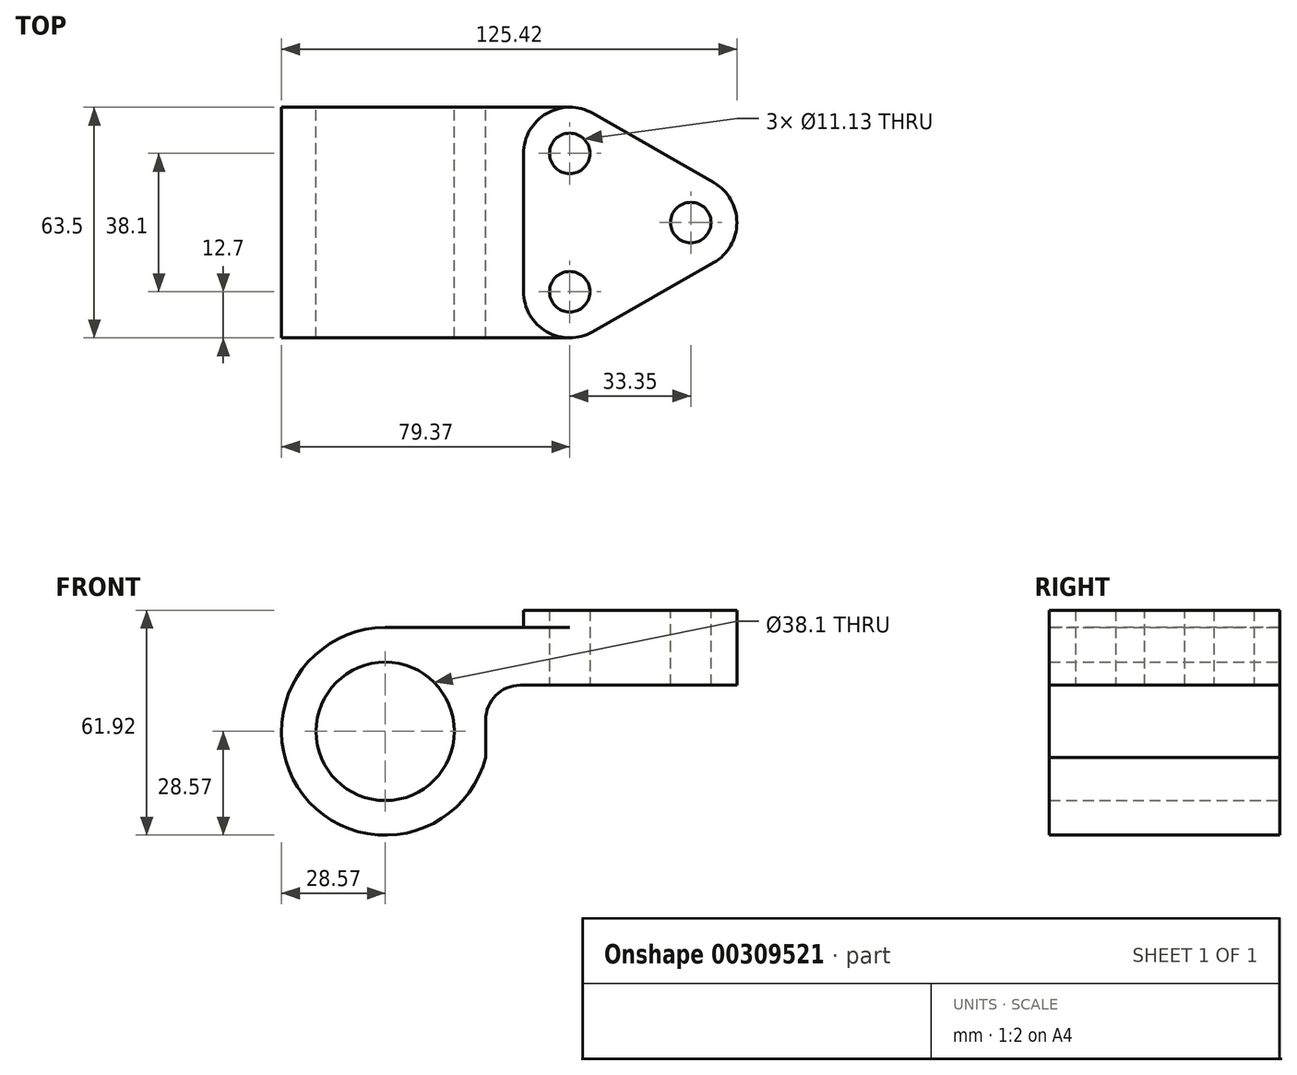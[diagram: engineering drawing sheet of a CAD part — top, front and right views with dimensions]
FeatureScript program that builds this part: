
annotation { "Feature Type Name" : "Feature", "Feature Type Description" : "" }
export const myFeature = defineFeature(function(context is Context, id is Id, definition is map)
    precondition{}
    {
        {
            var Q0;
            Q0=qCreatedBy(makeId("Front.planeOp"),FACE);
            var sketch = newSketch(context, id + "F0", { "sketchPlane" : qUnion([Q0])});
            skCircle(sketch, "E0", {"center": v(0, 0) * mm, "radius": 19.05 * mm});
            skArc(sketch, "E1", {"start": v(0, 28.58) * mm, "mid": v(-22.6, -17.5) * mm, "end": v(27.67, -7.14) * mm});
            skLineSegment(sketch, "E2.top", {"start": v(0, 28.57) * mm, "end": v(69.85, 28.57) * mm});
            skLineSegment(sketch, "E2.right", {"start": v(69.85, 12.7) * mm, "end": v(69.85, 28.57) * mm});
            skLineSegment(sketch, "E3", {"start": v(69.85, 12.7) * mm, "end": v(37.2, 12.7) * mm});
            skLineSegment(sketch, "E4", {"start": v(27.67, 3.17) * mm, "end": v(27.67, -7.14) * mm});
            skPoint(sketch, "E5.visualSharp", {"position": v(27.67, 12.7) * mm});
            skArc(sketch, "E5.filletArc", {"start": v(37.2, 12.7) * mm, "mid": v(30.46, 9.91) * mm, "end": v(27.67, 3.17) * mm});
            skSolve(sketch);
        }
        {
            var Q0;
            Q0 = qSketchRegion(id + "F0", true);
            extrude(context, id + "F1", {"entities" : qUnion([Q0]), "depth" : 63.5 * mm});
        }
        {
            var Q0;
            Q0=makeQuery(id+"F1.opExtrude","SWEPT_FACE",FACE,{"disambiguationData":[OSD([sQuery(id+"F0.wireOp",EDGE,"E2.top")])]});
            var sketch = newSketch(context, id + "F2", { "sketchPlane" : qUnion([Q0])});
            skPoint(sketch, "E6", {"position": v(0, -31.75) * mm});
            skPoint(sketch, "E7", {"position": v(50.8, -31.75) * mm});
            skPoint(sketch, "E8", {"position": v(50.8, -63.5) * mm});
            skPoint(sketch, "E9", {"position": v(50.8, 0) * mm});
            skPoint(sketch, "E10", {"position": v(50.8, -12.7) * mm});
            skArc(sketch, "E11", {"start": v(57.1, -1.67) * mm, "mid": v(44.42, -1.72) * mm, "end": v(38.1, -12.7) * mm});
            skPoint(sketch, "E12", {"position": v(50.8, -50.8) * mm});
            skArc(sketch, "E13", {"start": v(38.1, -50.8) * mm, "mid": v(44.42, -61.78) * mm, "end": v(57.1, -61.83) * mm});
            skArc(sketch, "E14", {"start": v(90.45, -42.78) * mm, "mid": v(96.85, -31.75) * mm, "end": v(90.45, -20.72) * mm});
            skPoint(sketch, "E14.centerSnap0", {"position": v(69.85, -31.75) * mm});
            skLineSegment(sketch, "E15", {"start": v(57.1, -1.67) * mm, "end": v(90.45, -20.72) * mm});
            skLineSegment(sketch, "E16", {"start": v(90.45, -42.78) * mm, "end": v(57.1, -61.83) * mm});
            skLineSegment(sketch, "E17", {"start": v(38.1, -12.7) * mm, "end": v(38.1, -50.8) * mm});
            skCircle(sketch, "E18", {"center": v(84.15, -31.75) * mm, "radius": 5.56 * mm});
            skCircle(sketch, "E19", {"center": v(50.8, -12.7) * mm, "radius": 5.56 * mm});
            skCircle(sketch, "E20", {"center": v(50.8, -50.8) * mm, "radius": 5.56 * mm});
            skSolve(sketch);
        }
        {
            var Q0;
            Q0 = qSketchRegion(id + "F2", true);
            var Q1;
            Q1=makeQuery(id+"F2.imprint","IMPRINT",FACE,{"disambiguationData":[TD([[makeQuery(id+"F2.imprint","IMPRINT",EDGE,{"derivedFrom":sQuery(id+"F2.wireOp",EDGE,"E18")}),1.0]])]});
            extrude(context, id + "F3", {"entities" : qUnion([Q0, Q1]), "operationType" : NewBodyOperationType.ADD, "depth" : 4.78 * mm});
        }
        {
            var Q0;
            Q0 = qSketchRegion(id + "F2", true);
            extrude(context, id + "F4", {"entities" : qUnion([Q0]), "operationType" : NewBodyOperationType.ADD, "depth" : 4.78 * mm});
        }
        {
            var Q0;
            {var subQ2=sQuery(id+"F0.wireOp",EDGE,"E2.top");var subQ3=makeQuery(id+"F1.opExtrude","SWEPT_FACE",FACE,{"disambiguationData":[OSD([subQ2])]});var subQ4=sQuery(id+"F2.wireOp",EDGE,"E15");Q0=makeQuery(id+"F3.boolean.opBoolean","SPLIT",FACE,{"disambiguationData":[TD([makeQuery(id+"F3.opExtrude","SWEPT_FACE",FACE,{"disambiguationData":[OSD([subQ4])]})])],"derivedFrom":subQ3});}
            var Q1;
            {var subQ0=sQuery(id+"F2.wireOp",EDGE,"E16");var subQ3=sQuery(id+"F0.wireOp",EDGE,"E2.top");var subQ4=makeQuery(id+"F1.opExtrude","SWEPT_FACE",FACE,{"disambiguationData":[OSD([subQ3])]});Q1=makeQuery(id+"F3.boolean.opBoolean","SPLIT",FACE,{"disambiguationData":[TD([makeQuery(id+"F3.opExtrude","SWEPT_FACE",FACE,{"disambiguationData":[OSD([subQ0])]})])],"derivedFrom":subQ4});}
            extrude(context, id + "F5", {"entities" : qUnion([Q0, Q1]), "operationType" : NewBodyOperationType.REMOVE, "endBound" : BoundingType.UP_TO_NEXT, "oppositeDirection" : true, "depth" : 25.4 * mm});
        }
        {
            var Q0;
            Q0=makeQuery(id+"F3.boolean.opBoolean","SPLIT",FACE,{"disambiguationData":[TD([makeQuery(id+"F3.opExtrude","SWEPT_FACE",FACE,{"disambiguationData":[OSD([sQuery(id+"F2.wireOp",EDGE,"E19")])]})])],"derivedFrom":makeQuery(id+"F1.opExtrude","SWEPT_FACE",FACE,{"disambiguationData":[OSD([sQuery(id+"F0.wireOp",EDGE,"E2.top")])]})});
            var Q1;
            Q1=makeQuery(id+"F3.boolean.opBoolean","SPLIT",FACE,{"disambiguationData":[TD([makeQuery(id+"F3.opExtrude","SWEPT_FACE",FACE,{"disambiguationData":[OSD([sQuery(id+"F2.wireOp",EDGE,"E20")])]})])],"derivedFrom":makeQuery(id+"F1.opExtrude","SWEPT_FACE",FACE,{"disambiguationData":[OSD([sQuery(id+"F0.wireOp",EDGE,"E2.top")])]})});
            extrude(context, id + "F6", {"entities" : qUnion([Q0, Q1]), "operationType" : NewBodyOperationType.REMOVE, "oppositeDirection" : true, "depth" : 20.65 * mm});
        }
        {
            var Q0;
            Q0=makeQuery(id+"F3.opExtrude","CAP_FACE",FACE,{"disambiguationData":[OSD([sQuery(id+"F2.wireOp",EDGE,"E11"),sQuery(id+"F2.wireOp",EDGE,"E13"),sQuery(id+"F2.wireOp",EDGE,"E14"),sQuery(id+"F2.wireOp",EDGE,"E15"),sQuery(id+"F2.wireOp",EDGE,"E16"),sQuery(id+"F2.wireOp",EDGE,"E17"),sQuery(id+"F2.wireOp",EDGE,"E19"),sQuery(id+"F2.wireOp",EDGE,"E20")])],"isStart":false});
            var sketch = newSketch(context, id + "F7", { "sketchPlane" : qUnion([Q0])});
            skCircle(sketch, "E21", {"center": v(84.15, -31.75) * mm, "radius": 5.56 * mm});
            skSolve(sketch);
        }
        {
            var Q0;
            Q0 = qSketchRegion(id + "F7", true);
            extrude(context, id + "F8", {"entities" : qUnion([Q0]), "operationType" : NewBodyOperationType.REMOVE, "oppositeDirection" : true, "depth" : 20.65 * mm});
        }
        {
            var Q0;
            Q0=makeQuery(id+"F3.opExtrude","CAP_FACE",FACE,{"disambiguationData":[OSD([sQuery(id+"F2.wireOp",EDGE,"E11"),sQuery(id+"F2.wireOp",EDGE,"E13"),sQuery(id+"F2.wireOp",EDGE,"E14"),sQuery(id+"F2.wireOp",EDGE,"E15"),sQuery(id+"F2.wireOp",EDGE,"E16"),sQuery(id+"F2.wireOp",EDGE,"E17"),sQuery(id+"F2.wireOp",EDGE,"E19"),sQuery(id+"F2.wireOp",EDGE,"E20")])],"isStart":true});
            var Q1;
            Q1=makeQuery(id+"F1.opExtrude","SWEPT_FACE",FACE,{"disambiguationData":[OSD([sQuery(id+"F0.wireOp",EDGE,"E3")])]});
            extrude(context, id + "F9", {"entities" : qUnion([Q0]), "operationType" : NewBodyOperationType.ADD, "endBound" : BoundingType.UP_TO_SURFACE, "endBoundEntityFace" : qUnion([Q1]), "depth" : 25.4 * mm});
        }
    });
